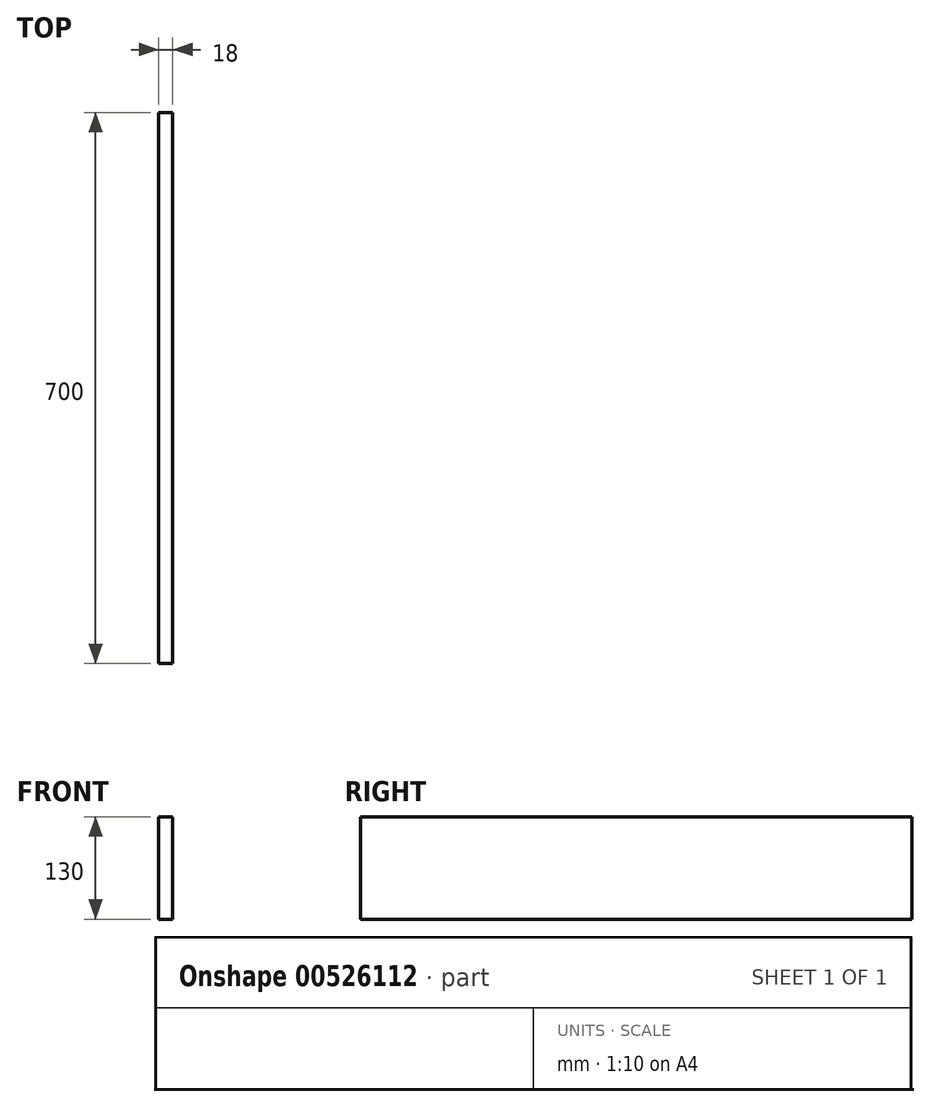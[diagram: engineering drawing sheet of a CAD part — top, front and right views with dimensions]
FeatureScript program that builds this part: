
annotation { "Feature Type Name" : "Feature", "Feature Type Description" : "" }
export const myFeature = defineFeature(function(context is Context, id is Id, definition is map)
    precondition{}
    {
        {
            var Q0;
            Q0=qCreatedBy(makeId("Right.planeOp"),FACE);
            var sketch = newSketch(context, id + "F0", { "sketchPlane" : qUnion([Q0])});
            skLineSegment(sketch, "E0.bottom", {"start": v(-350, 65) * mm, "end": v(350, 65) * mm});
            skLineSegment(sketch, "E0.top", {"start": v(-350, -65) * mm, "end": v(350, -65) * mm});
            skLineSegment(sketch, "E0.left", {"start": v(-350, 65) * mm, "end": v(-350, -65) * mm});
            skLineSegment(sketch, "E0.right", {"start": v(350, 65) * mm, "end": v(350, -65) * mm});
            skPoint(sketch, "E0.middle", {"position": v(0, 0) * mm});
            skSolve(sketch);
        }
        {
            var Q0;
            Q0=qSketchRegion(id+"F0",true);
            extrude(context, id + "F1", {"entities" : qUnion([Q0]), "depth" : 18 * mm, "offsetDistance" : 25 * mm});
        }
    });
